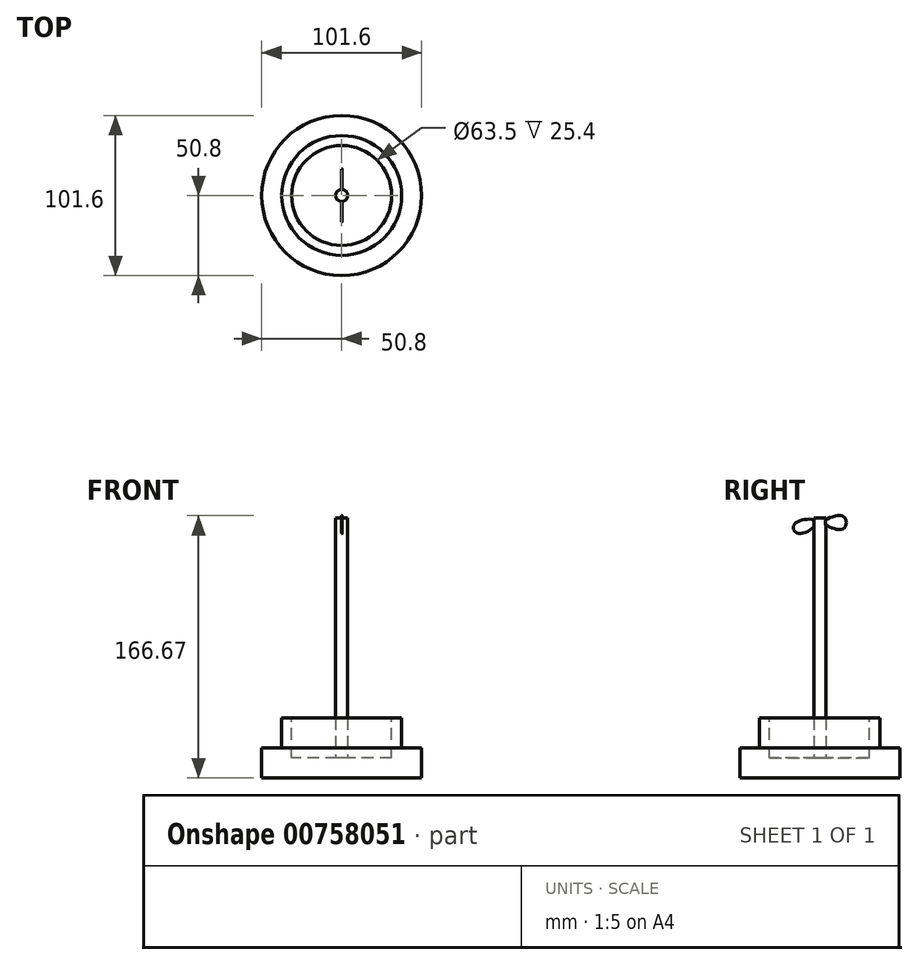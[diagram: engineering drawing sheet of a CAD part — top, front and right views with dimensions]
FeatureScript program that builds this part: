
annotation { "Feature Type Name" : "Feature", "Feature Type Description" : "" }
export const myFeature = defineFeature(function(context is Context, id is Id, definition is map)
    precondition{}
    {
        {
            var Q0;
            Q0=qCreatedBy(makeId("Top.planeOp"),FACE);
            var sketch = newSketch(context, id + "F0", { "sketchPlane" : qUnion([Q0])});
            skCircle(sketch, "E0", {"center": v(0, 0) * mm, "radius": 50.8 * mm});
            skSolve(sketch);
        }
        {
            var Q0;
            Q0 = qSketchRegion(id + "F0", true);
            extrude(context, id + "F1", {"entities" : qUnion([Q0]), "depth" : 19.05 * mm, "offsetDistance" : 25.4 * mm});
        }
        {
            var Q0;
            Q0=makeQuery(id+"F1.opExtrude","CAP_FACE",FACE,{"disambiguationData":[OSD([sQuery(id+"F0.wireOp",EDGE,"E0")])],"isStart":false});
            var sketch = newSketch(context, id + "F2", { "sketchPlane" : qUnion([Q0])});
            skCircle(sketch, "E1", {"center": v(0, 0) * mm, "radius": 38.1 * mm});
            skSolve(sketch);
        }
        {
            var Q0;
            Q0=makeQuery(id+"F2.imprint","IMPRINT",FACE,{"disambiguationData":[TD([[makeQuery(id+"F2.imprint","IMPRINT",EDGE,{"derivedFrom":sQuery(id+"F2.wireOp",EDGE,"E1")}),1.0]])]});
            extrude(context, id + "F3", {"entities" : qUnion([Q0]), "operationType" : NewBodyOperationType.ADD, "depth" : 19.05 * mm, "offsetDistance" : 25.4 * mm});
        }
        {
            var Q0;
            Q0=makeQuery(id+"F3.opExtrude","CAP_FACE",FACE,{"disambiguationData":[OSD([sQuery(id+"F2.wireOp",EDGE,"E1")])],"isStart":false});
            var sketch = newSketch(context, id + "F4", { "sketchPlane" : qUnion([Q0])});
            skCircle(sketch, "E2", {"center": v(0, 0) * mm, "radius": 31.75 * mm});
            skSolve(sketch);
        }
        {
            var Q0;
            Q0=makeQuery(id+"F4.imprint","IMPRINT",FACE,{"disambiguationData":[TD([[makeQuery(id+"F4.imprint","IMPRINT",EDGE,{"derivedFrom":sQuery(id+"F4.wireOp",EDGE,"E2")}),1.0]])]});
            extrude(context, id + "F5", {"entities" : qUnion([Q0]), "operationType" : NewBodyOperationType.REMOVE, "oppositeDirection" : true, "depth" : 25.4 * mm, "offsetDistance" : 25.4 * mm});
        }
        {
            var Q0;
            Q0=makeQuery(id+"F5.boolean.opBoolean","COPY",FACE,{"derivedFrom":makeQuery(id+"F5.opExtrude","CAP_FACE",FACE,{"disambiguationData":[OSD([sQuery(id+"F4.wireOp",EDGE,"E2")])],"isStart":false})});
            var sketch = newSketch(context, id + "F6", { "sketchPlane" : qUnion([Q0])});
            skCircle(sketch, "E3", {"center": v(0, 0) * mm, "radius": 3.81 * mm});
            skSolve(sketch);
        }
        {
            var Q0;
            Q0=makeQuery(id+"F6.imprint","IMPRINT",FACE,{"disambiguationData":[TD([[makeQuery(id+"F6.imprint","IMPRINT",EDGE,{"derivedFrom":sQuery(id+"F6.wireOp",EDGE,"E3")}),1.0]])]});
            extrude(context, id + "F7", {"entities" : qUnion([Q0]), "operationType" : NewBodyOperationType.ADD, "depth" : 152.4 * mm, "offsetDistance" : 25.4 * mm});
        }
        {
            var Q0;
            Q0=qCreatedBy(makeId("Right.planeOp"),FACE);
            var sketch = newSketch(context, id + "F8", { "sketchPlane" : qUnion([Q0])});
            skCircle(sketch, "E4", {"center": v(0, 163.01) * mm, "radius": 2.29 * mm});
            skFitSpline(sketch, "E5", {"points": [v(0.18, 165.3) * mm, v(-3.28, 178.58) * mm, v(2.42, 178.84) * mm, v(0.18, 165.3) * mm]});
            skFitSpline(sketch, "E6", {"points": [v(2.27, 162.76) * mm, v(14.88, 166.13) * mm, v(15.14, 158.34) * mm, v(3.2, 161.2) * mm, v(2.27, 162.76) * mm]});
            skFitSpline(sketch, "E7", {"points": [v(-2.29, 163.01) * mm, v(-16, 161.2) * mm, v(-12.88, 155.23) * mm, v(-2.29, 163.01) * mm]});
            skFitSpline(sketch, "E8", {"points": [v(1.39, 161.2) * mm, v(3.2, 148.74) * mm, v(-2.29, 148.74) * mm, v(-1.39, 161.2) * mm, v(1.39, 161.2) * mm]});
            skSolve(sketch);
        }
        {
            var Q0;
            {var subQ0=sQuery(id+"F8.wireOp",EDGE,"E6");var subQ1=sQuery(id+"F8.wireOp",EDGE,"E4");var subQ2=makeQuery(id+"F8.imprint","INTERSECT",VERTEX,{"disambiguationData":[OD(0.0)],"derivedFrom":[subQ1,subQ0]});Q0=makeQuery(id+"F8.imprint","IMPRINT",FACE,{"disambiguationData":[TD([[makeQuery(id+"F8.imprint","IMPRINT",EDGE,{"disambiguationData":[TD([[subQ2,-1.0]])],"derivedFrom":subQ1}),-1.0]])]});}
            var Q1;
            {var subQ0=sQuery(id+"F8.wireOp",EDGE,"E5");var subQ1=sQuery(id+"F8.wireOp",EDGE,"E4");var subQ2=makeQuery(id+"F8.imprint","INTERSECT",VERTEX,{"disambiguationData":[OD(0.0)],"derivedFrom":[subQ1,subQ0]});Q1=makeQuery(id+"F8.imprint","IMPRINT",FACE,{"disambiguationData":[TD([[makeQuery(id+"F8.imprint","IMPRINT",EDGE,{"disambiguationData":[TD([[subQ2,1.0]])],"derivedFrom":subQ1}),-1.0]])]});}
            var Q2;
            {var subQ0=sQuery(id+"F8.wireOp",EDGE,"E7");var subQ1=sQuery(id+"F8.wireOp",EDGE,"E4");var subQ2=makeQuery(id+"F8.imprint","INTERSECT",VERTEX,{"disambiguationData":[OD(0.0)],"derivedFrom":[subQ1,subQ0]});Q2=makeQuery(id+"F8.imprint","IMPRINT",FACE,{"disambiguationData":[TD([[makeQuery(id+"F8.imprint","IMPRINT",EDGE,{"disambiguationData":[TD([[subQ2,-1.0]])],"derivedFrom":subQ1}),-1.0]])]});}
            extrude(context, id + "F9", {"entities" : qUnion([Q0, Q1, Q2]), "operationType" : NewBodyOperationType.ADD, "depth" : 0.25 * mm, "offsetDistance" : 25.4 * mm});
        }
        {
            var Q0;
            Q0=qCreatedBy(makeId("Right.planeOp"),FACE);
            var sketch = newSketch(context, id + "F10", { "sketchPlane" : qUnion([Q0])});
            skLineSegment(sketch, "E9.bottom", {"start": v(-2.72, 52.4) * mm, "end": v(2.43, 52.4) * mm});
            skLineSegment(sketch, "E9.top", {"start": v(-2.72, 41.55) * mm, "end": v(2.43, 41.55) * mm});
            skLineSegment(sketch, "E9.left", {"start": v(-2.72, 52.4) * mm, "end": v(-2.72, 41.55) * mm});
            skLineSegment(sketch, "E9.right", {"start": v(2.43, 52.4) * mm, "end": v(2.43, 41.55) * mm});
            skLineSegment(sketch, "E10.bottom", {"start": v(-2, 50.88) * mm, "end": v(1.71, 50.88) * mm});
            skLineSegment(sketch, "E10.top", {"start": v(-2, 48.6) * mm, "end": v(1.71, 48.6) * mm});
            skLineSegment(sketch, "E10.left", {"start": v(-2, 50.88) * mm, "end": v(-2, 48.6) * mm});
            skLineSegment(sketch, "E10.right", {"start": v(1.71, 50.88) * mm, "end": v(1.71, 48.6) * mm});
            skLineSegment(sketch, "E11.bottom", {"start": v(-2.1, 47.12) * mm, "end": v(1.81, 47.12) * mm});
            skLineSegment(sketch, "E11.top", {"start": v(-2.1, 42.75) * mm, "end": v(1.81, 42.75) * mm});
            skLineSegment(sketch, "E11.left", {"start": v(-2.1, 47.12) * mm, "end": v(-2.1, 42.75) * mm});
            skLineSegment(sketch, "E11.right", {"start": v(1.81, 47.12) * mm, "end": v(1.81, 42.75) * mm});
            skSolve(sketch);
        }
        {
            var Q0;
            Q0=sQuery(id+"F10.wireOp",EDGE,"E10.bottom");
            var Q1;
            Q1=sQuery(id+"F10.wireOp",EDGE,"E10.right");
            var Q2;
            Q2=sQuery(id+"F10.wireOp",EDGE,"E10.top");
            var Q3;
            Q3=sQuery(id+"F10.wireOp",EDGE,"E10.left");
            var Q4;
            Q4=sQuery(id+"F10.wireOp",EDGE,"E9.bottom");
            var Q5;
            Q5=sQuery(id+"F10.wireOp",EDGE,"E9.left");
            var Q6;
            Q6=sQuery(id+"F10.wireOp",EDGE,"E9.right");
            var Q7;
            Q7=sQuery(id+"F10.wireOp",EDGE,"E11.bottom");
            var Q8;
            Q8=sQuery(id+"F10.wireOp",EDGE,"E11.top");
            var Q9;
            Q9=sQuery(id+"F10.wireOp",EDGE,"E11.right");
            var Q10;
            Q10=sQuery(id+"F10.wireOp",EDGE,"E11.left");
            var Q11;
            Q11=sQuery(id+"F10.wireOp",EDGE,"E9.top");
            extrude(context, id + "F11", {"bodyType" : ToolBodyType.SURFACE, "surfaceEntities" : qUnion([Q0, Q1, Q2, Q3, Q4, Q5, Q6, Q7, Q8, Q9, Q10, Q11]), "depth" : 0.5 * mm, "offsetDistance" : 25.4 * mm});
        }
    });
